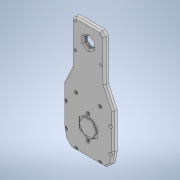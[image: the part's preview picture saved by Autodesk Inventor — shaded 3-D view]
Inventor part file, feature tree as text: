
AUTODESK INVENTOR PART (.ipt)
format: ipt  version: 2022 (Build 260153000, 153)  size: 466,944 bytes
history: native  units: in
note: dims shown in document units (in); Inventor stores cm internally (conversion verified against a paired STEP export)
features: extrude x14, sketch x12, projected_geometry x6, chamfer x3
ambient origin geometry x8: Origin, YZ Plane, XZ Plane, XY Plane, X Axis, Y Axis, Z Axis, Center Point
bodies: Solid1 (feature_tree)
feature tree (35):
  extrude  "Extrusion1"  Depth=0.7902in
  extrude  "Extrusion2"  Depth=0.1575in
  extrude  "Extrusion3"  Depth=0.1181in TaperAngle=0.0deg
  extrude  "Extrusion4"  Depth=0.5906in
  extrude  "Extrusion5"  Depth=0.5906in
  extrude  "Extrusion6"  Depth=1.5748in
  extrude  "Extrusion7"  Depth=0.0787in TaperAngle=0.0deg
  extrude  "Extrusion8"  TaperAngle=0.0deg  [1 undecoded]
  extrude  "Extrusion9"  Depth=0.0197in TaperAngle=0.0deg
  chamfer  "Chamfer4"  Distance=0.0197in Angle=45.0deg
  sketch  "Sketch11"  dims[d46=0.1358in d47=0.5497in]
  extrude  "Extrusion10"  Depth=0.5497in
  extrude  "Extrusion11"  Depth=0.3937in
  chamfer  "Chamfer6"  Distance=0.3937in
  sketch  "Sketch13"  dims[d56=0.0787in d57=0.0787in d58=45.0deg d61=0.3937in d62=0.0in d64=0.1181in d65=0.3937in d66=0.0in d67=0.3937in d68=0.0in d69=0.0787in d70=0.0787in d71=45.0deg]
  extrude  "Extrusion12"  Depth=0.3937in TaperAngle=0.0deg
  extrude  "Extrusion13"  Depth=0.0787in
  extrude  "Extrusion14"  Depth=0.3937in TaperAngle=0.0deg
  chamfer  "Chamfer7"  Distance=0.3937in
  sketch  "Sketch1"  dims[d0=2.5in d1=0.7902in]
  sketch  "Sketch2"  dims[d2=0.1181in d3=0.0in d8=0.1575in]
  sketch  "Sketch3"  dims[d11=0.1575in d12=0.1181in d13=0.0in]
  sketch  "Sketch5"  dims[d14=0.1181in d15=0.0in d16=0.5906in]
  sketch  "Sketch6"  dims[d17=0.1181in d18=0.0in d19=0.5906in]
  projected_geometry  "Projected Loop2"
  sketch  "Sketch7"  dims[d20=0.1575in d21=1.5748in]
  projected_geometry  "Projected Loop3"
  sketch  "Sketch8"  dims[d22=0.1181in d23=0.0in d27=0.0787in d28=0.0in]
  sketch  "Sketch9"  dims[d31=1.5748in d32=0.1181in d33=360.0deg d34=0.0in d35=0.0in]
  sketch  "Sketch10"  dims[d39=0.0197in d40=0.0in d41=0.0197in d42=0.0in d43=0.0197in d44=0.125in d45=45.0deg]
  projected_geometry  "Projected Loop4"
  projected_geometry  "Projected Loop5"
  sketch  "Sketch12"  dims[d48=0.3937in d49=0.0in d53=0.1181in d54=0.3937in d55=0.0in]
  projected_geometry  "Projected Loop6"
  projected_geometry  "Projected Loop7"
note: 1 required parameter value undecoded (feature->parameter linkage not recoverable at this tier; creation-order binding heuristic only, values carry confidence <= 0.55)
